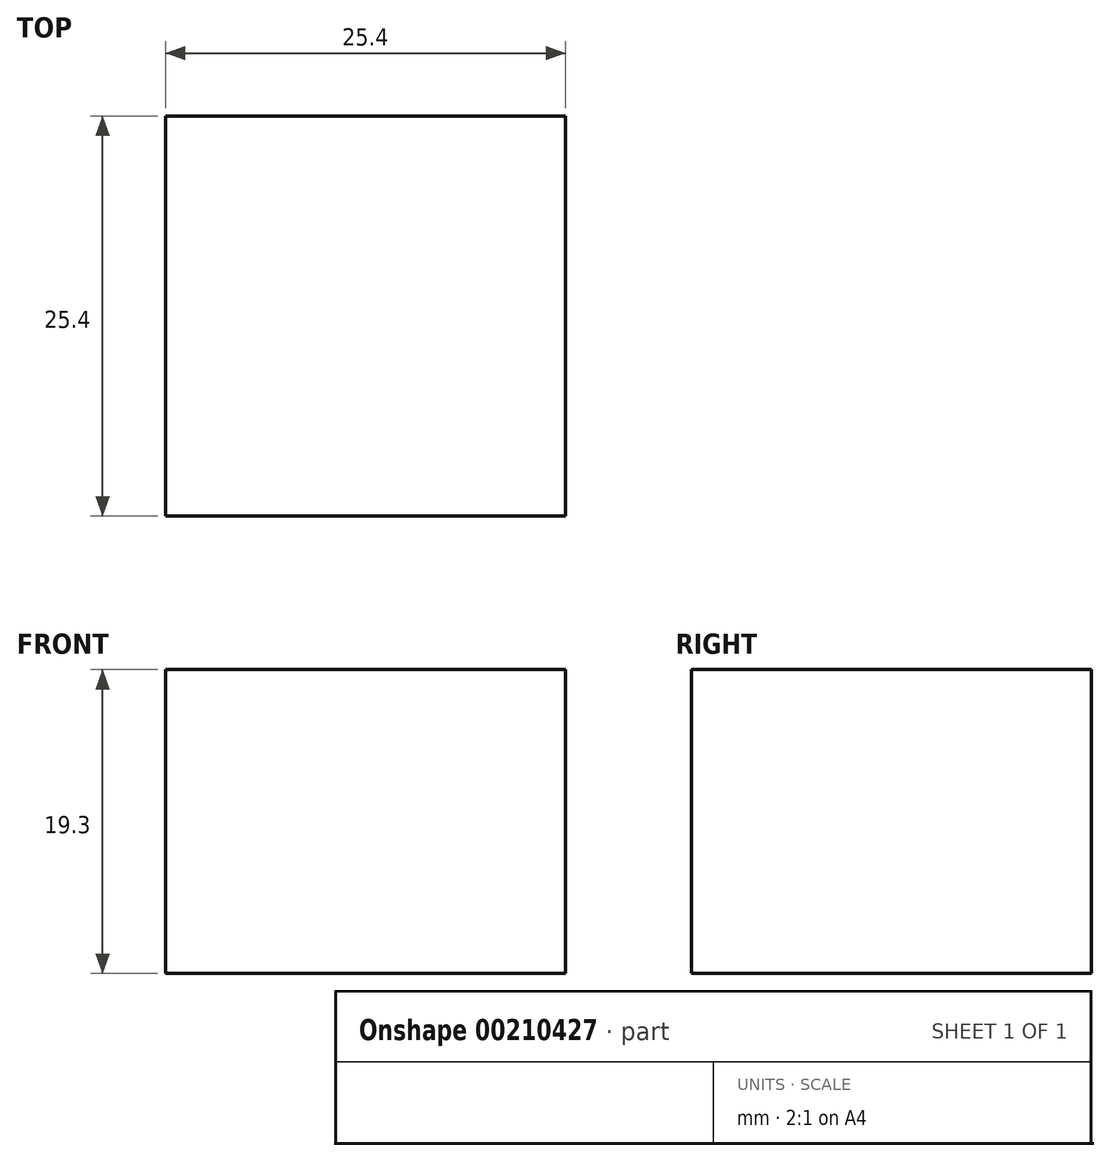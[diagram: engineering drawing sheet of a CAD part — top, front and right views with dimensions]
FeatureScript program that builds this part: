
annotation { "Feature Type Name" : "Feature", "Feature Type Description" : "" }
export const myFeature = defineFeature(function(context is Context, id is Id, definition is map)
    precondition{}
    {
        {
            var Q0;
            Q0=qCreatedBy(makeId("Top.planeOp"),FACE);
            var sketch = newSketch(context, id + "F0", { "sketchPlane" : qUnion([Q0])});
            skLineSegment(sketch, "E0.bottom", {"start": v(-109.12, 8.95) * mm, "end": v(-83.72, 8.95) * mm});
            skLineSegment(sketch, "E0.top", {"start": v(-109.12, -16.45) * mm, "end": v(-83.72, -16.45) * mm});
            skLineSegment(sketch, "E0.left", {"start": v(-109.12, 8.95) * mm, "end": v(-109.12, -16.45) * mm});
            skLineSegment(sketch, "E0.right", {"start": v(-83.72, 8.95) * mm, "end": v(-83.72, -16.45) * mm});
            skSolve(sketch);
        }
        {
            var Q0;
            Q0=makeQuery(id+"F0.imprint","IMPRINT",FACE,{"disambiguationData":[TD([[makeQuery(id+"F0.imprint","IMPRINT",EDGE,{"derivedFrom":sQuery(id+"F0.wireOp",EDGE,"E0.bottom")}),-1.0]])]});
            extrude(context, id + "F1", {"entities" : qUnion([Q0]), "depth" : 19.3 * mm});
        }
    });
